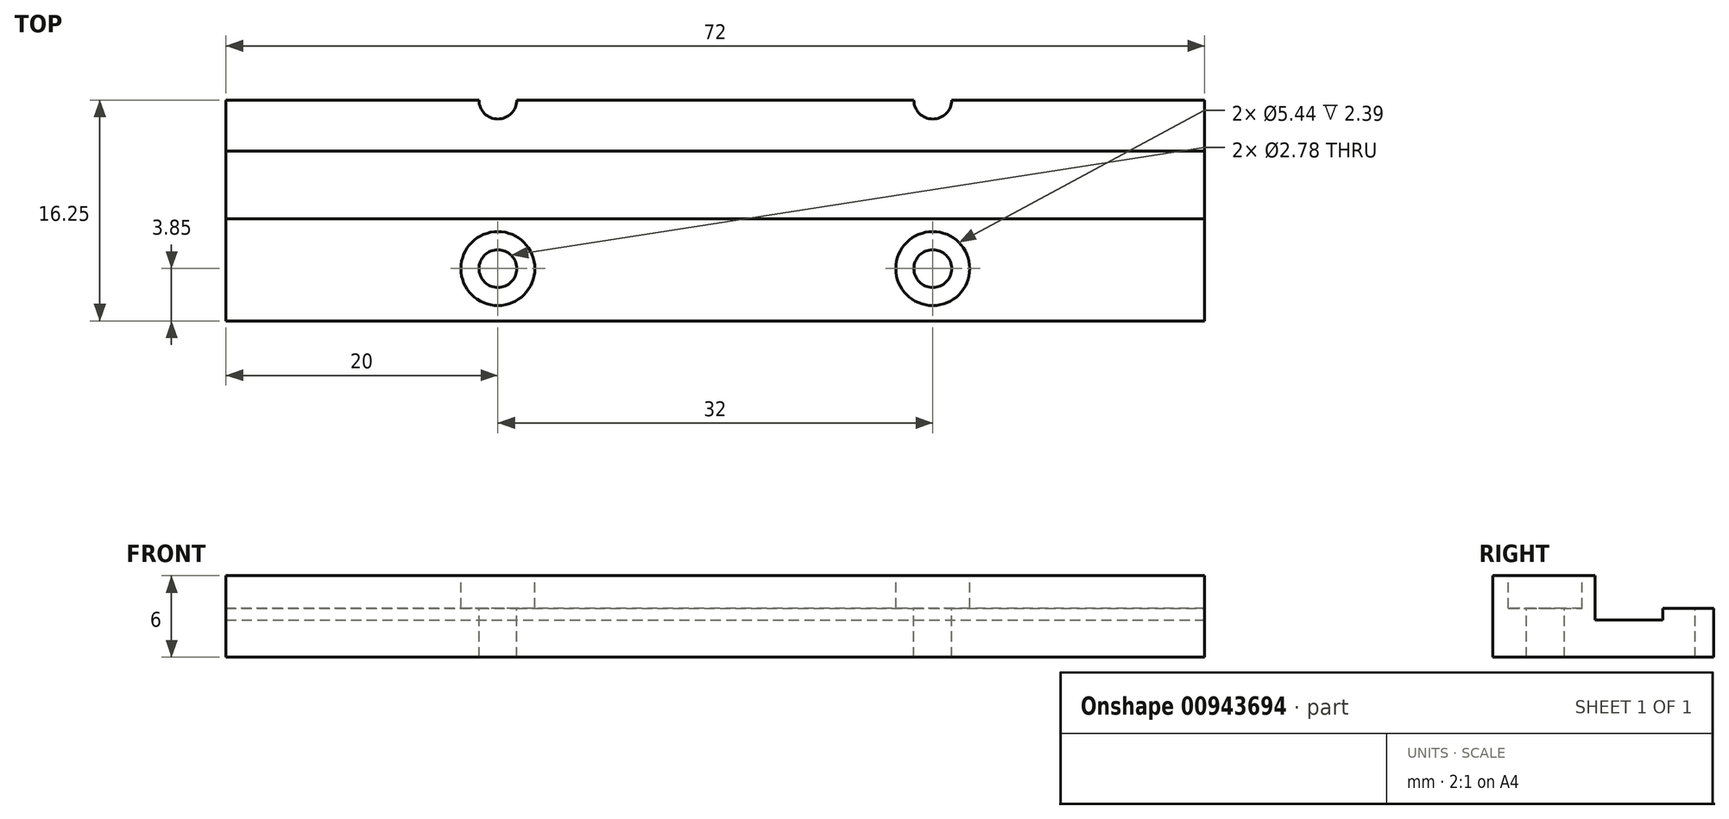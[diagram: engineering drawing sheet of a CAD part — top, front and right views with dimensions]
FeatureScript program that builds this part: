
annotation { "Feature Type Name" : "Feature", "Feature Type Description" : "" }
export const myFeature = defineFeature(function(context is Context, id is Id, definition is map)
    precondition{}
    {
        {
            var Q0;
            Q0=qCreatedBy(makeId("Top.planeOp"),FACE);
            var sketch = newSketch(context, id + "F0", { "sketchPlane" : qUnion([Q0])});
            skLineSegment(sketch, "E0.bottom", {"start": v(36, 10) * mm, "end": v(-36, 10) * mm});
            skLineSegment(sketch, "E0.top", {"start": v(36, -10) * mm, "end": v(-36, -10) * mm});
            skLineSegment(sketch, "E0.left", {"start": v(36, 10) * mm, "end": v(36, -10) * mm});
            skLineSegment(sketch, "E0.right", {"start": v(-36, 10) * mm, "end": v(-36, -10) * mm});
            skPoint(sketch, "E0.middle", {"position": v(0, 0) * mm});
            skSolve(sketch);
        }
        {
            var Q0;
            Q0 = qSketchRegion(id + "F0", true);
            extrude(context, id + "F1", {"entities" : qUnion([Q0]), "depth" : 6 * mm, "offsetDistance" : 25 * mm});
        }
        {
            var Q0;
            Q0=makeQuery(id+"F1.opExtrude","SWEPT_FACE",FACE,{"disambiguationData":[OSD([sQuery(id+"F0.wireOp",EDGE,"E0.left")])]});
            var sketch = newSketch(context, id + "F2", { "sketchPlane" : qUnion([Q0])});
            skLineSegment(sketch, "E1.bottom", {"start": v(2.5, 2.75) * mm, "end": v(-2.5, 2.75) * mm});
            skLineSegment(sketch, "E1.top", {"start": v(2.5, 9.25) * mm, "end": v(-2.5, 9.25) * mm});
            skLineSegment(sketch, "E1.left", {"start": v(2.5, 2.75) * mm, "end": v(2.5, 9.25) * mm});
            skLineSegment(sketch, "E1.right", {"start": v(-2.5, 2.75) * mm, "end": v(-2.5, 9.25) * mm});
            skPoint(sketch, "E1.middle", {"position": v(0, 6) * mm});
            skSolve(sketch);
        }
        {
            var Q0;
            Q0 = qSketchRegion(id + "F2", true);
            extrude(context, id + "F3", {"entities" : qUnion([Q0]), "operationType" : NewBodyOperationType.REMOVE, "oppositeDirection" : true, "depth" : 100 * mm, "offsetDistance" : 25 * mm});
        }
        {
            var Q0;
            {var subQ0=sQuery(id+"F0.wireOp",EDGE,"E0.bottom");var subQ1=sQuery(id+"F0.wireOp",EDGE,"E0.right");var subQ2=sQuery(id+"F0.wireOp",EDGE,"E0.left");Q0=makeQuery(id+"F3.boolean.opBoolean","SPLIT",FACE,{"disambiguationData":[TD([makeQuery(id+"F1.opExtrude","SWEPT_FACE",FACE,{"disambiguationData":[OSD([subQ0])]})])],"derivedFrom":makeQuery(id+"F1.opExtrude","CAP_FACE",FACE,{"disambiguationData":[OSD([subQ0,sQuery(id+"F0.wireOp",EDGE,"E0.top"),subQ2,subQ1])],"isStart":false})});}
            var sketch = newSketch(context, id + "F4", { "sketchPlane" : qUnion([Q0])});
            skLineSegment(sketch, "E2", {"start": v(-16, 10) * mm, "end": v(-16, -10) * mm});
            skLineSegment(sketch, "E3", {"start": v(16, 10) * mm, "end": v(16, -10) * mm});
            skLineSegment(sketch, "E4", {"start": v(-35.89, 0) * mm, "end": v(36.29, 0) * mm});
            skLineSegment(sketch, "E5", {"start": v(-36, 6.25) * mm, "end": v(36, 6.25) * mm});
            skLineSegment(sketch, "E6", {"start": v(-35.92, -6.15) * mm, "end": v(36.06, -6.15) * mm});
            skCircle(sketch, "E7", {"center": v(-16, -6.15) * mm, "radius": 1.39 * mm});
            skCircle(sketch, "E8", {"center": v(16, -6.15) * mm, "radius": 1.39 * mm});
            skCircle(sketch, "E9", {"center": v(16, 6.25) * mm, "radius": 1.39 * mm});
            skCircle(sketch, "E10", {"center": v(-16, 6.25) * mm, "radius": 1.39 * mm});
            skCircle(sketch, "E11", {"center": v(-16, 6.25) * mm, "radius": 2.72 * mm});
            skCircle(sketch, "E12", {"center": v(-16, -6.15) * mm, "radius": 2.72 * mm});
            skCircle(sketch, "E13", {"center": v(16, -6.15) * mm, "radius": 2.72 * mm});
            skCircle(sketch, "E14", {"center": v(16, 6.25) * mm, "radius": 2.72 * mm});
            skSolve(sketch);
        }
        {
            var Q0;
            {var subQ0=sQuery(id+"F4.wireOp",EDGE,"E11");var subQ1=sQuery(id+"F4.wireOp",EDGE,"E2");var subQ2=makeQuery(id+"F4.imprint","INTERSECT",VERTEX,{"disambiguationData":[OD(0.0)],"derivedFrom":[subQ1,subQ0]});Q0=makeQuery(id+"F4.imprint","IMPRINT",FACE,{"disambiguationData":[TD([[makeQuery(id+"F4.imprint","IMPRINT",EDGE,{"disambiguationData":[TD([[subQ2,-1.0]])],"derivedFrom":subQ1}),1.0]])]});}
            var Q1;
            {var subQ0=sQuery(id+"F4.wireOp",EDGE,"E10");var subQ1=sQuery(id+"F4.wireOp",EDGE,"E2");var subQ2=makeQuery(id+"F4.imprint","INTERSECT",VERTEX,{"disambiguationData":[OD(1.0)],"derivedFrom":[subQ1,subQ0]});Q1=makeQuery(id+"F4.imprint","IMPRINT",FACE,{"disambiguationData":[TD([[makeQuery(id+"F4.imprint","IMPRINT",EDGE,{"disambiguationData":[TD([[subQ2,-1.0]])],"derivedFrom":subQ1}),-1.0]])]});}
            var Q2;
            {var subQ0=sQuery(id+"F4.wireOp",EDGE,"E11");var subQ1=sQuery(id+"F4.wireOp",EDGE,"E2");var subQ2=makeQuery(id+"F4.imprint","INTERSECT",VERTEX,{"disambiguationData":[OD(0.0)],"derivedFrom":[subQ1,subQ0]});Q2=makeQuery(id+"F4.imprint","IMPRINT",FACE,{"disambiguationData":[TD([[makeQuery(id+"F4.imprint","IMPRINT",EDGE,{"disambiguationData":[TD([[subQ2,-1.0]])],"derivedFrom":subQ1}),-1.0]])]});}
            var Q3;
            {var subQ0=sQuery(id+"F4.wireOp",EDGE,"E10");var subQ1=sQuery(id+"F4.wireOp",EDGE,"E2");var subQ2=makeQuery(id+"F4.imprint","INTERSECT",VERTEX,{"disambiguationData":[OD(1.0)],"derivedFrom":[subQ1,subQ0]});Q3=makeQuery(id+"F4.imprint","IMPRINT",FACE,{"disambiguationData":[TD([[makeQuery(id+"F4.imprint","IMPRINT",EDGE,{"disambiguationData":[TD([[subQ2,-1.0]])],"derivedFrom":subQ1}),1.0]])]});}
            var Q4;
            {var subQ0=sQuery(id+"F4.wireOp",EDGE,"E12");var subQ1=sQuery(id+"F4.wireOp",EDGE,"E2");var subQ2=makeQuery(id+"F4.imprint","INTERSECT",VERTEX,{"disambiguationData":[OD(1.0)],"derivedFrom":[subQ1,subQ0]});Q4=makeQuery(id+"F4.imprint","IMPRINT",FACE,{"disambiguationData":[TD([[makeQuery(id+"F4.imprint","IMPRINT",EDGE,{"disambiguationData":[TD([[subQ2,-1.0]])],"derivedFrom":subQ1}),-1.0]])]});}
            var Q5;
            {var subQ0=sQuery(id+"F4.wireOp",EDGE,"E12");var subQ1=sQuery(id+"F4.wireOp",EDGE,"E2");var subQ2=makeQuery(id+"F4.imprint","INTERSECT",VERTEX,{"disambiguationData":[OD(1.0)],"derivedFrom":[subQ1,subQ0]});Q5=makeQuery(id+"F4.imprint","IMPRINT",FACE,{"disambiguationData":[TD([[makeQuery(id+"F4.imprint","IMPRINT",EDGE,{"disambiguationData":[TD([[subQ2,-1.0]])],"derivedFrom":subQ1}),1.0]])]});}
            var Q6;
            {var subQ0=sQuery(id+"F4.wireOp",EDGE,"E12");var subQ1=sQuery(id+"F4.wireOp",EDGE,"E2");var subQ2=makeQuery(id+"F4.imprint","INTERSECT",VERTEX,{"disambiguationData":[OD(0.0)],"derivedFrom":[subQ1,subQ0]});Q6=makeQuery(id+"F4.imprint","IMPRINT",FACE,{"disambiguationData":[TD([[makeQuery(id+"F4.imprint","IMPRINT",EDGE,{"disambiguationData":[TD([[subQ2,1.0]])],"derivedFrom":subQ1}),1.0]])]});}
            var Q7;
            {var subQ0=sQuery(id+"F4.wireOp",EDGE,"E12");var subQ1=sQuery(id+"F4.wireOp",EDGE,"E2");var subQ2=makeQuery(id+"F4.imprint","INTERSECT",VERTEX,{"disambiguationData":[OD(0.0)],"derivedFrom":[subQ1,subQ0]});Q7=makeQuery(id+"F4.imprint","IMPRINT",FACE,{"disambiguationData":[TD([[makeQuery(id+"F4.imprint","IMPRINT",EDGE,{"disambiguationData":[TD([[subQ2,1.0]])],"derivedFrom":subQ1}),-1.0]])]});}
            var Q8;
            {var subQ0=sQuery(id+"F4.wireOp",EDGE,"E13");var subQ1=sQuery(id+"F4.wireOp",EDGE,"E3");var subQ2=makeQuery(id+"F4.imprint","INTERSECT",VERTEX,{"disambiguationData":[OD(1.0)],"derivedFrom":[subQ1,subQ0]});Q8=makeQuery(id+"F4.imprint","IMPRINT",FACE,{"disambiguationData":[TD([[makeQuery(id+"F4.imprint","IMPRINT",EDGE,{"disambiguationData":[TD([[subQ2,-1.0]])],"derivedFrom":subQ1}),-1.0]])]});}
            var Q9;
            {var subQ0=sQuery(id+"F4.wireOp",EDGE,"E13");var subQ1=sQuery(id+"F4.wireOp",EDGE,"E3");var subQ2=makeQuery(id+"F4.imprint","INTERSECT",VERTEX,{"disambiguationData":[OD(1.0)],"derivedFrom":[subQ1,subQ0]});Q9=makeQuery(id+"F4.imprint","IMPRINT",FACE,{"disambiguationData":[TD([[makeQuery(id+"F4.imprint","IMPRINT",EDGE,{"disambiguationData":[TD([[subQ2,-1.0]])],"derivedFrom":subQ1}),1.0]])]});}
            var Q10;
            {var subQ0=sQuery(id+"F4.wireOp",EDGE,"E13");var subQ1=sQuery(id+"F4.wireOp",EDGE,"E3");var subQ2=makeQuery(id+"F4.imprint","INTERSECT",VERTEX,{"disambiguationData":[OD(0.0)],"derivedFrom":[subQ1,subQ0]});Q10=makeQuery(id+"F4.imprint","IMPRINT",FACE,{"disambiguationData":[TD([[makeQuery(id+"F4.imprint","IMPRINT",EDGE,{"disambiguationData":[TD([[subQ2,1.0]])],"derivedFrom":subQ1}),1.0]])]});}
            var Q11;
            {var subQ0=sQuery(id+"F4.wireOp",EDGE,"E13");var subQ1=sQuery(id+"F4.wireOp",EDGE,"E3");var subQ2=makeQuery(id+"F4.imprint","INTERSECT",VERTEX,{"disambiguationData":[OD(0.0)],"derivedFrom":[subQ1,subQ0]});Q11=makeQuery(id+"F4.imprint","IMPRINT",FACE,{"disambiguationData":[TD([[makeQuery(id+"F4.imprint","IMPRINT",EDGE,{"disambiguationData":[TD([[subQ2,1.0]])],"derivedFrom":subQ1}),-1.0]])]});}
            var Q12;
            {var subQ0=sQuery(id+"F4.wireOp",EDGE,"E9");var subQ1=sQuery(id+"F4.wireOp",EDGE,"E3");var subQ2=makeQuery(id+"F4.imprint","INTERSECT",VERTEX,{"disambiguationData":[OD(1.0)],"derivedFrom":[subQ1,subQ0]});Q12=makeQuery(id+"F4.imprint","IMPRINT",FACE,{"disambiguationData":[TD([[makeQuery(id+"F4.imprint","IMPRINT",EDGE,{"disambiguationData":[TD([[subQ2,-1.0]])],"derivedFrom":subQ1}),-1.0]])]});}
            var Q13;
            {var subQ0=sQuery(id+"F4.wireOp",EDGE,"E14");var subQ1=sQuery(id+"F4.wireOp",EDGE,"E3");var subQ2=makeQuery(id+"F4.imprint","INTERSECT",VERTEX,{"disambiguationData":[OD(0.0)],"derivedFrom":[subQ1,subQ0]});Q13=makeQuery(id+"F4.imprint","IMPRINT",FACE,{"disambiguationData":[TD([[makeQuery(id+"F4.imprint","IMPRINT",EDGE,{"disambiguationData":[TD([[subQ2,-1.0]])],"derivedFrom":subQ1}),1.0]])]});}
            var Q14;
            {var subQ0=sQuery(id+"F4.wireOp",EDGE,"E9");var subQ1=sQuery(id+"F4.wireOp",EDGE,"E3");var subQ2=makeQuery(id+"F4.imprint","INTERSECT",VERTEX,{"disambiguationData":[OD(1.0)],"derivedFrom":[subQ1,subQ0]});Q14=makeQuery(id+"F4.imprint","IMPRINT",FACE,{"disambiguationData":[TD([[makeQuery(id+"F4.imprint","IMPRINT",EDGE,{"disambiguationData":[TD([[subQ2,-1.0]])],"derivedFrom":subQ1}),1.0]])]});}
            var Q15;
            {var subQ0=sQuery(id+"F4.wireOp",EDGE,"E14");var subQ1=sQuery(id+"F4.wireOp",EDGE,"E3");var subQ2=makeQuery(id+"F4.imprint","INTERSECT",VERTEX,{"disambiguationData":[OD(0.0)],"derivedFrom":[subQ1,subQ0]});Q15=makeQuery(id+"F4.imprint","IMPRINT",FACE,{"disambiguationData":[TD([[makeQuery(id+"F4.imprint","IMPRINT",EDGE,{"disambiguationData":[TD([[subQ2,-1.0]])],"derivedFrom":subQ1}),-1.0]])]});}
            extrude(context, id + "F5", {"entities" : qUnion([Q0, Q1, Q2, Q3, Q4, Q5, Q6, Q7, Q8, Q9, Q10, Q11, Q12, Q13, Q14, Q15]), "operationType" : NewBodyOperationType.REMOVE, "oppositeDirection" : true, "depth" : 2.4 * mm, "offsetDistance" : 25 * mm});
        }
        {
            var Q0;
            {var subQ0=sQuery(id+"F0.wireOp",EDGE,"E0.bottom");var subQ1=sQuery(id+"F0.wireOp",EDGE,"E0.right");var subQ2=sQuery(id+"F0.wireOp",EDGE,"E0.left");Q0=makeQuery(id+"F5.boolean.opBoolean","SPLIT",FACE,{"disambiguationData":[TD([makeQuery(id+"F5.opExtrude","SWEPT_FACE",FACE,{"disambiguationData":[OSD([sQuery(id+"F4.wireOp",EDGE,"E10")])]})])],"derivedFrom":makeQuery(id+"F3.boolean.opBoolean","SPLIT",FACE,{"disambiguationData":[TD([makeQuery(id+"F1.opExtrude","SWEPT_FACE",FACE,{"disambiguationData":[OSD([subQ0])]})])],"derivedFrom":makeQuery(id+"F1.opExtrude","CAP_FACE",FACE,{"disambiguationData":[OSD([subQ0,sQuery(id+"F0.wireOp",EDGE,"E0.top"),subQ2,subQ1])],"isStart":false})})});}
            var Q1;
            {var subQ0=sQuery(id+"F0.wireOp",EDGE,"E0.top");var subQ1=sQuery(id+"F0.wireOp",EDGE,"E0.left");var subQ2=sQuery(id+"F0.wireOp",EDGE,"E0.right");Q1=makeQuery(id+"F5.boolean.opBoolean","SPLIT",FACE,{"disambiguationData":[TD([makeQuery(id+"F5.opExtrude","SWEPT_FACE",FACE,{"disambiguationData":[OSD([sQuery(id+"F4.wireOp",EDGE,"E7")])]})])],"derivedFrom":makeQuery(id+"F3.boolean.opBoolean","SPLIT",FACE,{"disambiguationData":[TD([makeQuery(id+"F1.opExtrude","SWEPT_FACE",FACE,{"disambiguationData":[OSD([subQ0])]})])],"derivedFrom":makeQuery(id+"F1.opExtrude","CAP_FACE",FACE,{"disambiguationData":[OSD([sQuery(id+"F0.wireOp",EDGE,"E0.bottom"),subQ0,subQ1,subQ2])],"isStart":false})})});}
            var Q2;
            {var subQ0=sQuery(id+"F0.wireOp",EDGE,"E0.top");var subQ1=sQuery(id+"F0.wireOp",EDGE,"E0.left");var subQ2=sQuery(id+"F0.wireOp",EDGE,"E0.right");Q2=makeQuery(id+"F5.boolean.opBoolean","SPLIT",FACE,{"disambiguationData":[TD([makeQuery(id+"F5.opExtrude","SWEPT_FACE",FACE,{"disambiguationData":[OSD([sQuery(id+"F4.wireOp",EDGE,"E8")])]})])],"derivedFrom":makeQuery(id+"F3.boolean.opBoolean","SPLIT",FACE,{"disambiguationData":[TD([makeQuery(id+"F1.opExtrude","SWEPT_FACE",FACE,{"disambiguationData":[OSD([subQ0])]})])],"derivedFrom":makeQuery(id+"F1.opExtrude","CAP_FACE",FACE,{"disambiguationData":[OSD([sQuery(id+"F0.wireOp",EDGE,"E0.bottom"),subQ0,subQ1,subQ2])],"isStart":false})})});}
            var Q3;
            {var subQ0=sQuery(id+"F0.wireOp",EDGE,"E0.bottom");var subQ1=sQuery(id+"F0.wireOp",EDGE,"E0.right");var subQ2=sQuery(id+"F0.wireOp",EDGE,"E0.left");Q3=makeQuery(id+"F5.boolean.opBoolean","SPLIT",FACE,{"disambiguationData":[TD([makeQuery(id+"F5.opExtrude","SWEPT_FACE",FACE,{"disambiguationData":[OSD([sQuery(id+"F4.wireOp",EDGE,"E9")])]})])],"derivedFrom":makeQuery(id+"F3.boolean.opBoolean","SPLIT",FACE,{"disambiguationData":[TD([makeQuery(id+"F1.opExtrude","SWEPT_FACE",FACE,{"disambiguationData":[OSD([subQ0])]})])],"derivedFrom":makeQuery(id+"F1.opExtrude","CAP_FACE",FACE,{"disambiguationData":[OSD([subQ0,sQuery(id+"F0.wireOp",EDGE,"E0.top"),subQ2,subQ1])],"isStart":false})})});}
            extrude(context, id + "F6", {"entities" : qUnion([Q0, Q1, Q2, Q3]), "operationType" : NewBodyOperationType.REMOVE, "oppositeDirection" : true, "depth" : 25 * mm, "offsetDistance" : 25 * mm});
        }
    });
